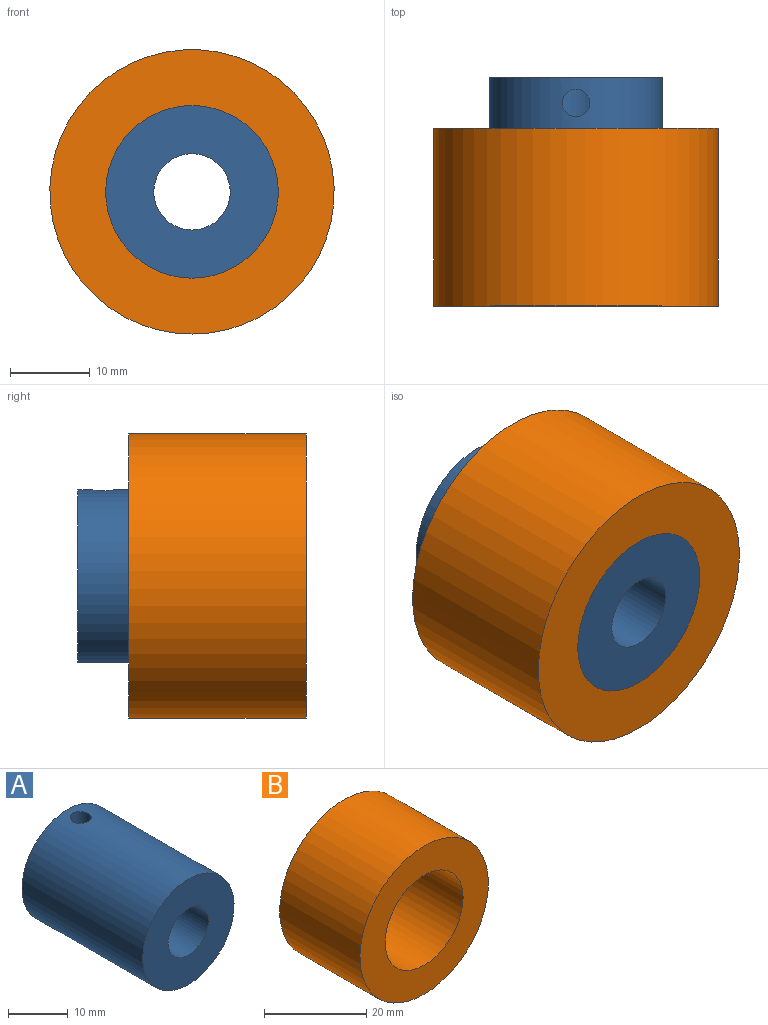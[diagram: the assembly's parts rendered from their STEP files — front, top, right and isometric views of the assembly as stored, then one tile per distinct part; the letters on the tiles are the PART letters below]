
ASSEMBLY  parts=2 mates=1
PART A: 5 faces, bbox 21.6x28.6x21.6 mm
  f0: cylinder r=4.78mm len=28.58mm, axis (0,1,0), area 847.8mm2, adj f2,f3,f4
  f1: cylinder r=10.79mm len=28.58mm, axis (0,1,0), area 1928.7mm2, adj f2,f3,f4
  f2: plane 21.59x21.59mm, normal (0,-1,0), area 294.5mm2, adj f0,f1
  f3: plane 21.59x21.59mm, normal (0,1,0), area 294.5mm2, adj f0,f1
  f4: cylinder r=1.73mm len=6.34mm, axis (0,0,1), area 66.3mm2, adj f0,f1
PART B: 4 faces, bbox 35.6x22.2x35.6 mm
  f0: cylinder r=10.79mm len=22.23mm, axis (0,1,0), area 1507.5mm2, adj f2,f3
  f1: cylinder r=17.78mm len=35.56mm, axis (0,1,0), area 2482.9mm2, adj f2,f3
  f2: plane 35.56x35.56mm, normal (0,-1,0), area 627.1mm2, adj f0,f1
  f3: plane 35.56x35.56mm, normal (0,1,0), area 627.1mm2, adj f0,f1
PLACE A t=(-5.53,7.46,-0.7)mm
PLACE B t=(-5.53,1.11,-0.7)mm
MATE fastened B.f0 <-> A.f0  axis (0,-1,0) through (-5.53,-21.12,-0.7)mm
